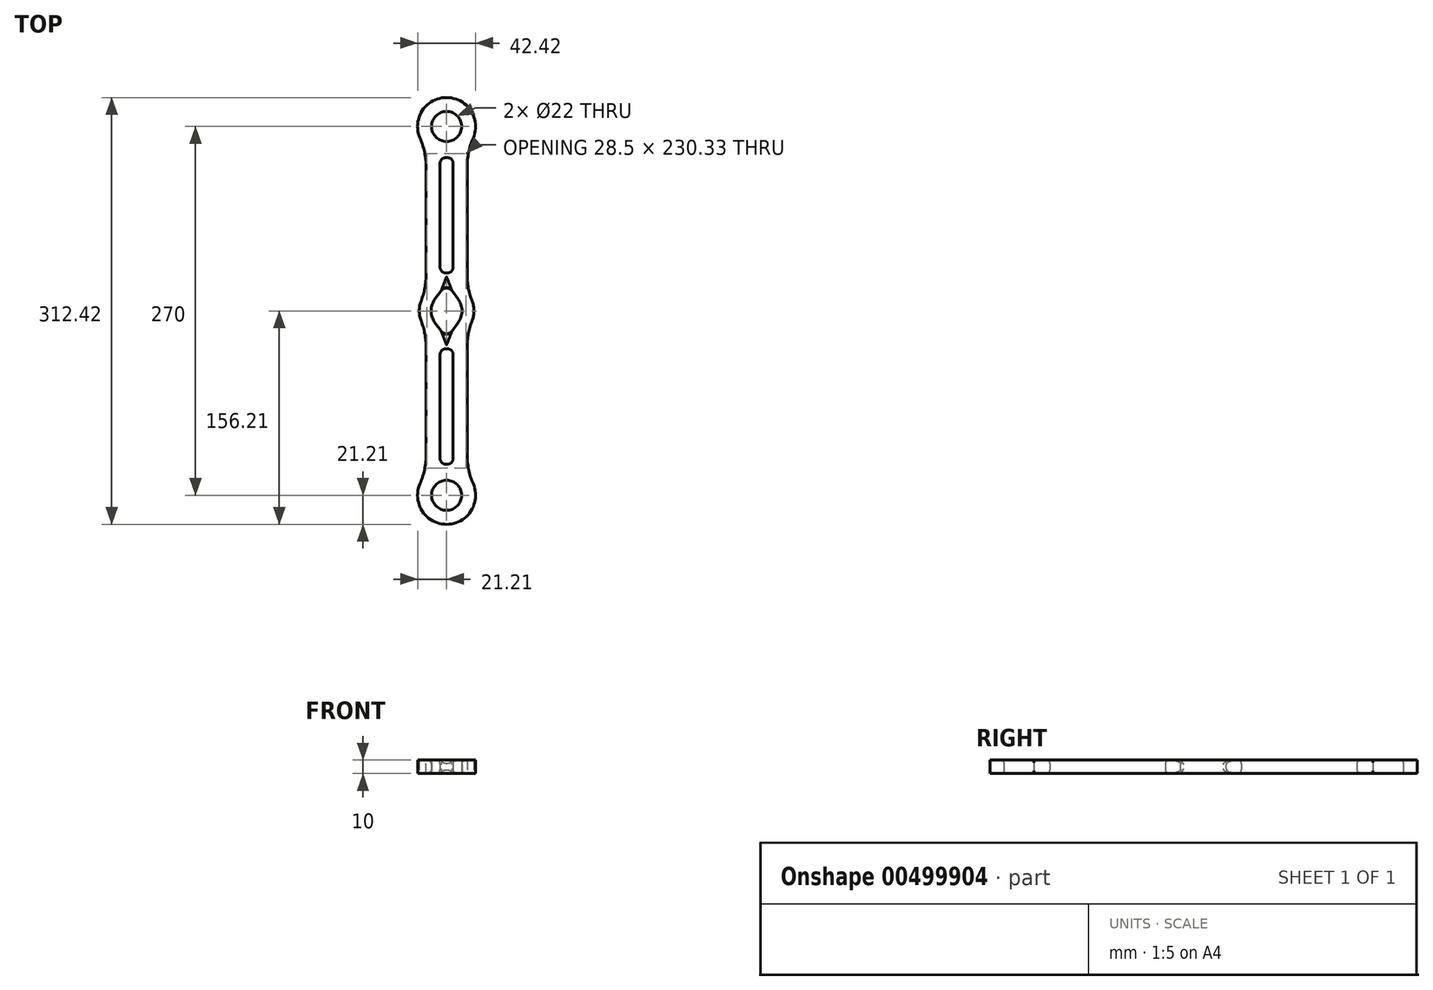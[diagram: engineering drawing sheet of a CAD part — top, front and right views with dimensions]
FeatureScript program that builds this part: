
annotation { "Feature Type Name" : "Feature", "Feature Type Description" : "" }
export const myFeature = defineFeature(function(context is Context, id is Id, definition is map)
    precondition{}
    {
        {
            var Q0;
            Q0=qCreatedBy(makeId("Top.planeOp"),FACE);
            var sketch = newSketch(context, id + "F0", { "sketchPlane" : qUnion([Q0])});
            skLineSegment(sketch, "E0.bottom", {"start": v(0, 0) * mm, "end": v(30, 0) * mm});
            skLineSegment(sketch, "E0.top", {"start": v(0, -300) * mm, "end": v(30, -300) * mm});
            skLineSegment(sketch, "E0.left", {"start": v(0, 0) * mm, "end": v(0, -300) * mm});
            skLineSegment(sketch, "E0.right", {"start": v(30, 0) * mm, "end": v(30, -300) * mm});
            skLineSegment(sketch, "E1.bottom", {"start": v(0, -300) * mm, "end": v(30, -300) * mm, "construction": true});
            skLineSegment(sketch, "E1.top", {"start": v(0, -270) * mm, "end": v(30, -270) * mm, "construction": true});
            skLineSegment(sketch, "E1.left", {"start": v(0, -300) * mm, "end": v(0, -270) * mm, "construction": true});
            skLineSegment(sketch, "E1.right", {"start": v(30, -300) * mm, "end": v(30, -270) * mm, "construction": true});
            skCircle(sketch, "E2", {"center": v(15, -285) * mm, "radius": 11 * mm});
            skPoint(sketch, "E2.centerSnap0", {"position": v(0, -285) * mm});
            skPoint(sketch, "E2.centerSnap1", {"position": v(15, -270) * mm});
            skCircle(sketch, "E3", {"center": v(15, -285) * mm, "radius": 21.21 * mm});
            skLineSegment(sketch, "E4.top", {"start": v(0, -30) * mm, "end": v(30, -30) * mm});
            skLineSegment(sketch, "E4.left", {"start": v(0, 0) * mm, "end": v(0, -30) * mm});
            skLineSegment(sketch, "E4.right", {"start": v(30, 0) * mm, "end": v(30, -30) * mm});
            skCircle(sketch, "E5", {"center": v(15, -15) * mm, "radius": 11 * mm});
            skPoint(sketch, "E5.centerSnap0", {"position": v(30, -15) * mm});
            skPoint(sketch, "E5.centerSnap1", {"position": v(15, 0) * mm});
            skCircle(sketch, "E6", {"center": v(15, -15) * mm, "radius": 21.21 * mm});
            skCircle(sketch, "E7", {"center": v(15, -150) * mm, "radius": 20 * mm});
            skPoint(sketch, "E7.centerSnap0", {"position": v(0, -150) * mm});
            skLineSegment(sketch, "E8", {"start": v(15, -150) * mm, "end": v(15, -130) * mm});
            skLineSegment(sketch, "E9", {"start": v(15, -150) * mm, "end": v(15, -170) * mm});
            skLineSegment(sketch, "E10", {"start": v(15, -150) * mm, "end": v(30, -150) * mm});
            skLineSegment(sketch, "E11", {"start": v(15, -150) * mm, "end": v(0, -150) * mm});
            skLineSegment(sketch, "E12", {"start": v(15, -170) * mm, "end": v(23.25, -159) * mm});
            skLineSegment(sketch, "E13", {"start": v(23.25, -141) * mm, "end": v(15, -130) * mm});
            skLineSegment(sketch, "E14", {"start": v(15, -130) * mm, "end": v(6.75, -141) * mm});
            skLineSegment(sketch, "E15", {"start": v(6.75, -159) * mm, "end": v(15, -170) * mm});
            skPoint(sketch, "E16.visualSharp", {"position": v(30, -150) * mm});
            skArc(sketch, "E16.filletArc", {"start": v(23.25, -159) * mm, "mid": v(26.25, -150) * mm, "end": v(23.25, -141) * mm});
            skArc(sketch, "E17.filletArc", {"start": v(6.75, -141) * mm, "mid": v(3.75, -150) * mm, "end": v(6.75, -159) * mm});
            skLineSegment(sketch, "E18", {"start": v(15, -170) * mm, "end": v(15, -270) * mm, "construction": true});
            skLineSegment(sketch, "E19.bottom", {"start": v(15.73, -177.84) * mm, "end": v(14.27, -177.84) * mm});
            skLineSegment(sketch, "E19.top", {"start": v(15.73, -262.16) * mm, "end": v(14.27, -262.16) * mm});
            skLineSegment(sketch, "E19.left", {"start": v(19.73, -181.84) * mm, "end": v(19.73, -258.16) * mm});
            skLineSegment(sketch, "E19.right", {"start": v(10.27, -181.84) * mm, "end": v(10.27, -258.16) * mm});
            skPoint(sketch, "E19.middle", {"position": v(15, -220) * mm});
            skPoint(sketch, "E20.visualSharp", {"position": v(19.73, -177.84) * mm});
            skArc(sketch, "E20.filletArc", {"start": v(19.73, -181.84) * mm, "mid": v(18.56, -179) * mm, "end": v(15.73, -177.84) * mm});
            skPoint(sketch, "E21.visualSharp", {"position": v(10.27, -177.84) * mm});
            skArc(sketch, "E21.filletArc", {"start": v(14.27, -177.84) * mm, "mid": v(11.44, -179) * mm, "end": v(10.27, -181.84) * mm});
            skPoint(sketch, "E22.visualSharp", {"position": v(19.73, -262.16) * mm});
            skArc(sketch, "E22.filletArc", {"start": v(15.73, -262.16) * mm, "mid": v(18.56, -261) * mm, "end": v(19.73, -258.16) * mm});
            skPoint(sketch, "E23.visualSharp", {"position": v(10.27, -262.16) * mm});
            skArc(sketch, "E23.filletArc", {"start": v(10.27, -258.16) * mm, "mid": v(11.44, -261) * mm, "end": v(14.27, -262.16) * mm});
            skLineSegment(sketch, "E24", {"start": v(15, -130) * mm, "end": v(15, -30) * mm, "construction": true});
            skLineSegment(sketch, "E25.bottom", {"start": v(15.73, -37.84) * mm, "end": v(14.27, -37.84) * mm});
            skLineSegment(sketch, "E25.top", {"start": v(15.73, -122.16) * mm, "end": v(14.27, -122.16) * mm});
            skLineSegment(sketch, "E25.left", {"start": v(19.73, -41.84) * mm, "end": v(19.73, -118.16) * mm});
            skLineSegment(sketch, "E25.right", {"start": v(10.27, -41.84) * mm, "end": v(10.27, -118.16) * mm});
            skPoint(sketch, "E25.middle", {"position": v(15, -80) * mm});
            skPoint(sketch, "E26.visualSharp", {"position": v(19.73, -37.84) * mm});
            skArc(sketch, "E26.filletArc", {"start": v(19.73, -41.84) * mm, "mid": v(18.56, -39) * mm, "end": v(15.73, -37.84) * mm});
            skPoint(sketch, "E27.visualSharp", {"position": v(19.73, -122.16) * mm});
            skArc(sketch, "E27.filletArc", {"start": v(15.73, -122.16) * mm, "mid": v(18.56, -121) * mm, "end": v(19.73, -118.16) * mm});
            skPoint(sketch, "E28.visualSharp", {"position": v(10.27, -122.16) * mm});
            skArc(sketch, "E28.filletArc", {"start": v(10.27, -118.16) * mm, "mid": v(11.44, -121) * mm, "end": v(14.27, -122.16) * mm});
            skPoint(sketch, "E29.visualSharp", {"position": v(10.27, -37.84) * mm});
            skArc(sketch, "E29.filletArc", {"start": v(14.27, -37.84) * mm, "mid": v(11.44, -39) * mm, "end": v(10.27, -41.84) * mm});
            skSolve(sketch);
        }
        {
            var Q0;
            Q0 = qSketchRegion(id + "F0", true);
            extrude(context, id + "F1", {"entities" : qUnion([Q0]), "depth" : 10 * mm});
        }
        {
            var Q0;
            {var subQ0=sQuery(id+"F0.wireOp",EDGE,"E7");var subQ1=sQuery(id+"F0.wireOp",EDGE,"E0.right");Q0=makeQuery(id+"F1.opExtrude","SWEPT_EDGE",EDGE,{"disambiguationData":[OSD([subQ1,subQ0]),TDD([makeQuery(id+"F0.imprint","INTERSECT",VERTEX,{"disambiguationData":[OD(1.0)],"derivedFrom":[subQ1,subQ0]})])]});}
            var Q1;
            {var subQ0=sQuery(id+"F0.wireOp",EDGE,"E7");var subQ1=sQuery(id+"F0.wireOp",EDGE,"E0.right");Q1=makeQuery(id+"F1.opExtrude","SWEPT_EDGE",EDGE,{"disambiguationData":[OSD([subQ1,subQ0]),TDD([makeQuery(id+"F0.imprint","INTERSECT",VERTEX,{"disambiguationData":[OD(0.0)],"derivedFrom":[subQ1,subQ0]})])]});}
            var Q2;
            {var subQ0=sQuery(id+"F0.wireOp",EDGE,"E7");var subQ1=sQuery(id+"F0.wireOp",EDGE,"E0.left");Q2=makeQuery(id+"F1.opExtrude","SWEPT_EDGE",EDGE,{"disambiguationData":[OSD([subQ1,subQ0]),TDD([makeQuery(id+"F0.imprint","INTERSECT",VERTEX,{"disambiguationData":[OD(0.0)],"derivedFrom":[subQ1,subQ0]})])]});}
            var Q3;
            {var subQ0=sQuery(id+"F0.wireOp",EDGE,"E7");var subQ1=sQuery(id+"F0.wireOp",EDGE,"E0.left");Q3=makeQuery(id+"F1.opExtrude","SWEPT_EDGE",EDGE,{"disambiguationData":[OSD([subQ1,subQ0]),TDD([makeQuery(id+"F0.imprint","INTERSECT",VERTEX,{"disambiguationData":[OD(1.0)],"derivedFrom":[subQ1,subQ0]})])]});}
            var Q4;
            Q4=makeQuery(id+"F1.opExtrude","SWEPT_EDGE",EDGE,{"disambiguationData":[OSD([sQuery(id+"F0.wireOp",EDGE,"E0.left"),sQuery(id+"F0.wireOp",EDGE,"E3")])]});
            var Q5;
            Q5=makeQuery(id+"F1.opExtrude","SWEPT_EDGE",EDGE,{"disambiguationData":[OSD([sQuery(id+"F0.wireOp",EDGE,"E0.right"),sQuery(id+"F0.wireOp",EDGE,"E4.top"),sQuery(id+"F0.wireOp",EDGE,"E4.right"),sQuery(id+"F0.wireOp",EDGE,"E6")])]});
            var Q6;
            Q6=makeQuery(id+"F1.opExtrude","SWEPT_EDGE",EDGE,{"disambiguationData":[OSD([sQuery(id+"F0.wireOp",EDGE,"E0.left"),sQuery(id+"F0.wireOp",EDGE,"E4.top"),sQuery(id+"F0.wireOp",EDGE,"E4.left"),sQuery(id+"F0.wireOp",EDGE,"E6")])]});
            var Q7;
            Q7=makeQuery(id+"F1.opExtrude","SWEPT_EDGE",EDGE,{"disambiguationData":[OSD([sQuery(id+"F0.wireOp",EDGE,"E0.right"),sQuery(id+"F0.wireOp",EDGE,"E3")])]});
            fillet(context, id + "F2", {"entities" : qUnion([Q0, Q1, Q2, Q3, Q4, Q5, Q6, Q7]), "radius" : 53.6 * mm, "tangentPropagation" : true, "allowEdgeOverflow" : false});
        }
        {
            var Q0;
            Q0=makeQuery(id+"F1.opExtrude","CAP_EDGE",EDGE,{"disambiguationData":[OSD([sQuery(id+"F0.wireOp",EDGE,"E13")])],"isStart":false});
            var Q1;
            Q1=makeQuery(id+"F1.opExtrude","CAP_EDGE",EDGE,{"disambiguationData":[OSD([sQuery(id+"F0.wireOp",EDGE,"E14")])],"isStart":false});
            var Q2;
            {var subQ0=sQuery(id+"F0.wireOp",EDGE,"E0.left");Q2=makeQuery(id+"F1.opExtrude","CAP_EDGE",EDGE,{"disambiguationData":[OSD([subQ0]),TDD([makeQuery(id+"F0.imprint","IMPRINT",EDGE,{"disambiguationData":[TD([[makeQuery(id+"F0.imprint","INTERSECT",VERTEX,{"disambiguationData":[OD(1.0)],"derivedFrom":[subQ0,sQuery(id+"F0.wireOp",EDGE,"E7")]}),-1.0]])],"derivedFrom":subQ0})])],"isStart":false});}
            var Q3;
            {var subQ0=sQuery(id+"F0.wireOp",EDGE,"E0.right");Q3=makeQuery(id+"F1.opExtrude","CAP_EDGE",EDGE,{"disambiguationData":[OSD([subQ0]),TDD([makeQuery(id+"F0.imprint","IMPRINT",EDGE,{"disambiguationData":[TD([[makeQuery(id+"F0.imprint","INTERSECT",VERTEX,{"disambiguationData":[OD(0.0)],"derivedFrom":[subQ0,sQuery(id+"F0.wireOp",EDGE,"E7")]}),1.0]])],"derivedFrom":subQ0})])],"isStart":true});}
            var Q4;
            Q4=makeQuery(id+"F1.opExtrude","CAP_EDGE",EDGE,{"disambiguationData":[OSD([sQuery(id+"F0.wireOp",EDGE,"E19.left")])],"isStart":false});
            var Q5;
            Q5=makeQuery(id+"F1.opExtrude","CAP_EDGE",EDGE,{"disambiguationData":[OSD([sQuery(id+"F0.wireOp",EDGE,"E25.left")])],"isStart":false});
            var Q6;
            Q6=makeQuery(id+"F1.opExtrude","CAP_EDGE",EDGE,{"disambiguationData":[OSD([sQuery(id+"F0.wireOp",EDGE,"E19.left")])],"isStart":true});
            var Q7;
            Q7=makeQuery(id+"F1.opExtrude","CAP_EDGE",EDGE,{"disambiguationData":[OSD([sQuery(id+"F0.wireOp",EDGE,"E25.left")])],"isStart":true});
            var Q8;
            Q8=makeQuery(id+"F1.opExtrude","CAP_EDGE",EDGE,{"disambiguationData":[OSD([sQuery(id+"F0.wireOp",EDGE,"E13")])],"isStart":true});
            var Q9;
            Q9=makeQuery(id+"F1.opExtrude","CAP_EDGE",EDGE,{"disambiguationData":[OSD([sQuery(id+"F0.wireOp",EDGE,"E14")])],"isStart":true});
            fillet(context, id + "F3", {"entities" : qUnion([Q0, Q1, Q2, Q3, Q4, Q5, Q6, Q7, Q8, Q9]), "radius" : 3 * mm, "tangentPropagation" : true, "allowEdgeOverflow" : false});
        }
        {
            var Q0;
            Q0=makeQuery(id+"F1.opExtrude","SWEPT_EDGE",EDGE,{"disambiguationData":[OSD([sQuery(id+"F0.wireOp",EDGE,"E7"),sQuery(id+"F0.wireOp",EDGE,"E9"),sQuery(id+"F0.wireOp",EDGE,"E12"),sQuery(id+"F0.wireOp",EDGE,"E15")])]});
            var Q1;
            Q1=makeQuery(id+"F1.opExtrude","SWEPT_EDGE",EDGE,{"disambiguationData":[OSD([sQuery(id+"F0.wireOp",EDGE,"E7"),sQuery(id+"F0.wireOp",EDGE,"E8"),sQuery(id+"F0.wireOp",EDGE,"E13"),sQuery(id+"F0.wireOp",EDGE,"E14")])]});
            fillet(context, id + "F4", {"entities" : qUnion([Q0, Q1]), "radius" : 5 * mm, "tangentPropagation" : true, "allowEdgeOverflow" : false});
        }
        {
            var Q0;
            Q0=makeQuery(id+"F1.opExtrude","CAP_EDGE",EDGE,{"disambiguationData":[OSD([sQuery(id+"F0.wireOp",EDGE,"E2")])],"isStart":false});
            var Q1;
            Q1=makeQuery(id+"F1.opExtrude","CAP_EDGE",EDGE,{"disambiguationData":[OSD([sQuery(id+"F0.wireOp",EDGE,"E2")])],"isStart":true});
            var Q2;
            Q2=makeQuery(id+"F1.opExtrude","CAP_EDGE",EDGE,{"disambiguationData":[OSD([sQuery(id+"F0.wireOp",EDGE,"E5")])],"isStart":false});
            var Q3;
            Q3=makeQuery(id+"F1.opExtrude","CAP_EDGE",EDGE,{"disambiguationData":[OSD([sQuery(id+"F0.wireOp",EDGE,"E5")])],"isStart":true});
            fillet(context, id + "F5", {"entities" : qUnion([Q0, Q1, Q2, Q3]), "radius" : 2 * mm, "tangentPropagation" : true, "allowEdgeOverflow" : false});
        }
    });
